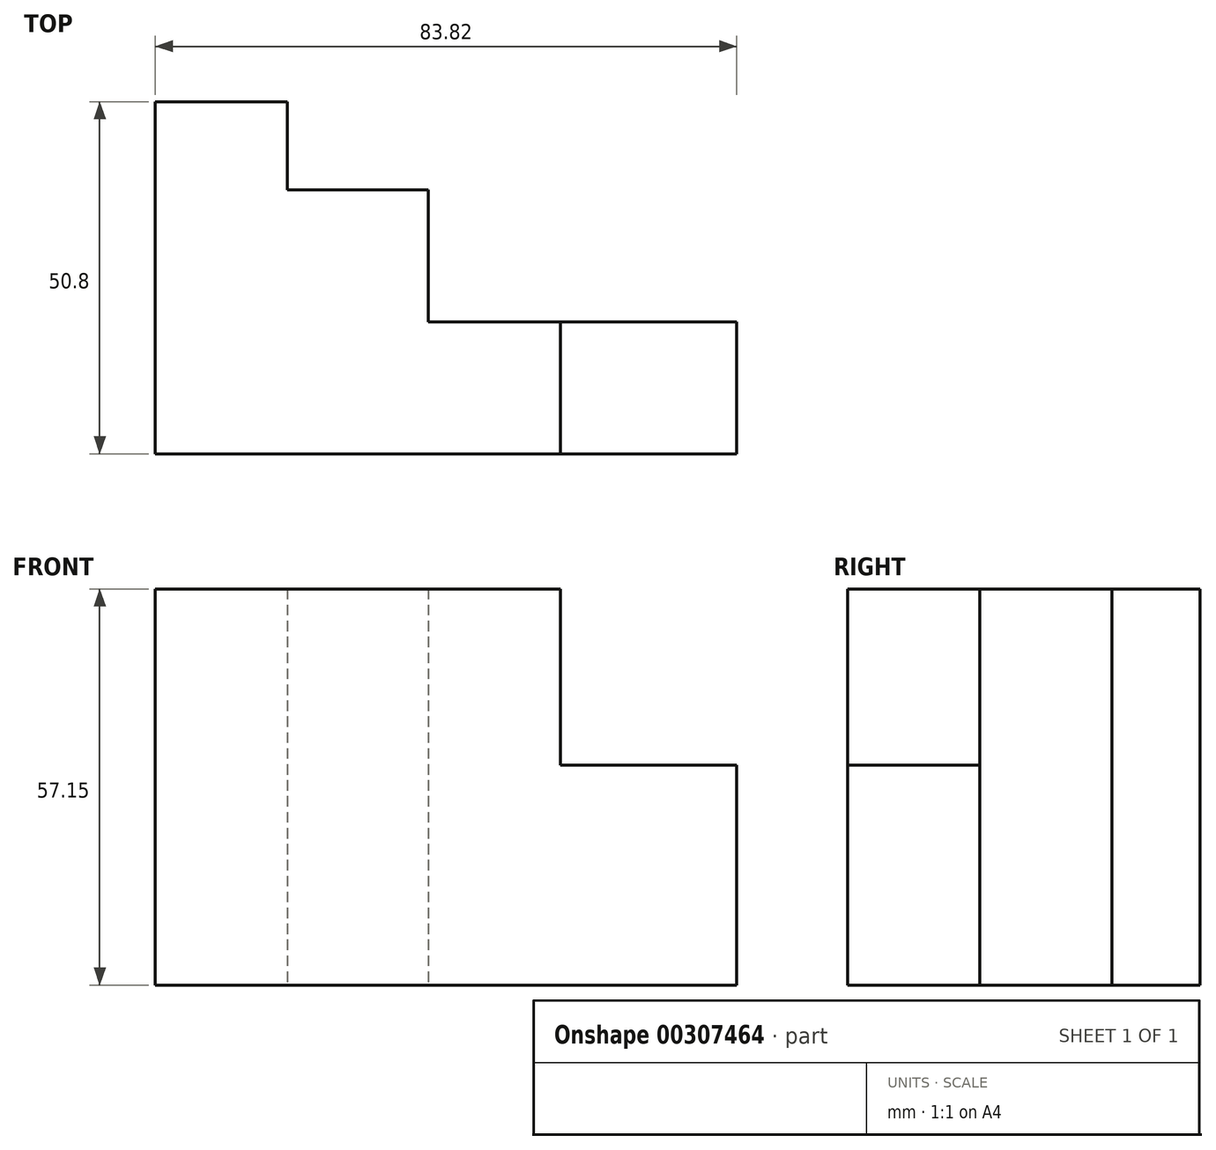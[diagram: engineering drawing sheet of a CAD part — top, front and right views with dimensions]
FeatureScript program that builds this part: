
annotation { "Feature Type Name" : "Feature", "Feature Type Description" : "" }
export const myFeature = defineFeature(function(context is Context, id is Id, definition is map)
    precondition{}
    {
        {
            var Q0;
            Q0=qCreatedBy(makeId("Top.planeOp"),FACE);
            var sketch = newSketch(context, id + "F0", { "sketchPlane" : qUnion([Q0])});
            skLineSegment(sketch, "E0", {"start": v(0, 0) * mm, "end": v(0, 50.8) * mm});
            skLineSegment(sketch, "E1", {"start": v(0, 50.8) * mm, "end": v(19.05, 50.8) * mm});
            skLineSegment(sketch, "E2", {"start": v(19.05, 50.8) * mm, "end": v(19.05, 38.1) * mm});
            skLineSegment(sketch, "E3", {"start": v(19.05, 38.1) * mm, "end": v(39.37, 38.1) * mm});
            skLineSegment(sketch, "E4", {"start": v(39.37, 38.1) * mm, "end": v(39.37, 19.05) * mm});
            skLineSegment(sketch, "E5", {"start": v(39.37, 19.05) * mm, "end": v(58.42, 19.05) * mm});
            skLineSegment(sketch, "E6", {"start": v(58.42, 19.05) * mm, "end": v(58.42, 0) * mm});
            skLineSegment(sketch, "E7", {"start": v(58.42, 0) * mm, "end": v(0, 0) * mm});
            skSolve(sketch);
        }
        {
            var Q0;
            Q0 = qSketchRegion(id + "F0", true);
            extrude(context, id + "F1", {"entities" : qUnion([Q0]), "depth" : 57.15 * mm});
        }
        {
            var Q0;
            Q0=makeQuery(id+"F1.opExtrude","SWEPT_FACE",FACE,{"disambiguationData":[OSD([sQuery(id+"F0.wireOp",EDGE,"E6")])]});
            var sketch = newSketch(context, id + "F2", { "sketchPlane" : qUnion([Q0])});
            skLineSegment(sketch, "E8.bottom", {"start": v(0, 0) * mm, "end": v(19.05, 0) * mm});
            skLineSegment(sketch, "E8.top", {"start": v(0, 31.75) * mm, "end": v(19.05, 31.75) * mm});
            skLineSegment(sketch, "E8.left", {"start": v(0, 0) * mm, "end": v(0, 31.75) * mm});
            skLineSegment(sketch, "E8.right", {"start": v(19.05, 0) * mm, "end": v(19.05, 31.75) * mm});
            skSolve(sketch);
        }
        {
            var Q0;
            Q0 = qSketchRegion(id + "F2", true);
            extrude(context, id + "F3", {"entities" : qUnion([Q0]), "operationType" : NewBodyOperationType.ADD, "depth" : 25.4 * mm});
        }
    });
